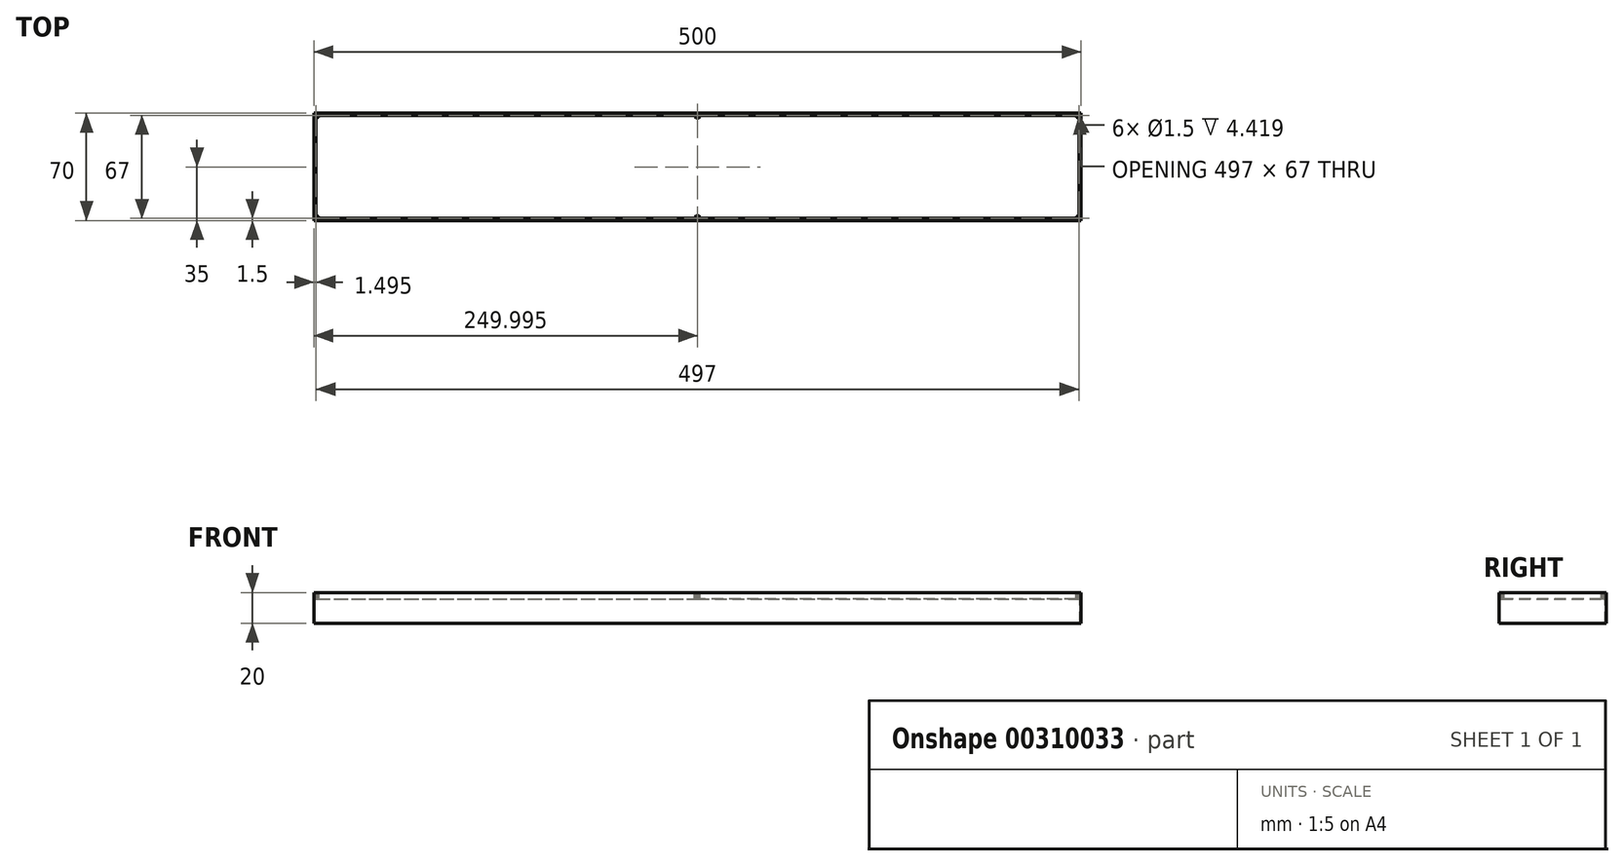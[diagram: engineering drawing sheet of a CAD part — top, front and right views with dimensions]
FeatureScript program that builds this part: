
annotation { "Feature Type Name" : "Feature", "Feature Type Description" : "" }
export const myFeature = defineFeature(function(context is Context, id is Id, definition is map)
    precondition{}
    {
        {
            var Q0;
            Q0=qCreatedBy(makeId("Front.planeOp"),FACE);
            var sketch = newSketch(context, id + "F0", { "sketchPlane" : qUnion([Q0])});
            skLineSegment(sketch, "E0.bottom", {"start": v(0.32, 0.32) * mm, "end": v(500.32, 0.32) * mm});
            skLineSegment(sketch, "E0.top", {"start": v(0.32, -19.68) * mm, "end": v(500.32, -19.68) * mm});
            skLineSegment(sketch, "E0.left", {"start": v(0.32, 0.32) * mm, "end": v(0.32, -19.68) * mm});
            skLineSegment(sketch, "E0.right", {"start": v(500.32, 0.32) * mm, "end": v(500.32, -19.68) * mm});
            skSolve(sketch);
        }
        {
            var Q0;
            Q0=makeQuery(id+"F0.imprint","IMPRINT",FACE,{"disambiguationData":[TD([[makeQuery(id+"F0.imprint","IMPRINT",EDGE,{"derivedFrom":sQuery(id+"F0.wireOp",EDGE,"E0.bottom")}),-1.0]])]});
            extrude(context, id + "F1", {"entities" : qUnion([Q0]), "depth" : 70 * mm});
        }
        {
            var Q0;
            Q0=qCreatedBy(makeId("Top.planeOp"),FACE);
            var sketch = newSketch(context, id + "F2", { "sketchPlane" : qUnion([Q0])});
            skLineSegment(sketch, "E1.1", {"start": v(498.82, -66.75) * mm, "end": v(498.82, -3.25) * mm});
            skLineSegment(sketch, "E1.3", {"start": v(1.82, -3.25) * mm, "end": v(1.82, -66.75) * mm});
            skCircle(sketch, "E2", {"center": v(1.82, -1.5) * mm, "radius": 0.75 * mm});
            skCircle(sketch, "E3", {"center": v(1.82, -68.5) * mm, "radius": 0.75 * mm});
            skCircle(sketch, "E4", {"center": v(250.32, -68.5) * mm, "radius": 0.75 * mm});
            skCircle(sketch, "E5", {"center": v(250.32, -1.5) * mm, "radius": 0.75 * mm});
            skCircle(sketch, "E6", {"center": v(498.82, -1.5) * mm, "radius": 0.75 * mm});
            skCircle(sketch, "E7", {"center": v(498.82, -68.5) * mm, "radius": 0.75 * mm});
            skArc(sketch, "E8.trimOffspring", {"start": v(497.07, -1.5) * mm, "mid": v(497.58, -2.74) * mm, "end": v(498.82, -3.25) * mm});
            skLineSegment(sketch, "E9.trimOffspring", {"start": v(497.07, -1.5) * mm, "end": v(252.07, -1.5) * mm});
            skArc(sketch, "E10.0", {"start": v(498.82, -66.75) * mm, "mid": v(497.58, -67.26) * mm, "end": v(497.07, -68.5) * mm});
            skArc(sketch, "E11.0", {"start": v(252.07, -68.5) * mm, "mid": v(250.32, -66.75) * mm, "end": v(248.57, -68.5) * mm});
            skLineSegment(sketch, "E12.trimOffspring", {"start": v(252.07, -68.5) * mm, "end": v(497.07, -68.5) * mm});
            skArc(sketch, "E13.0", {"start": v(3.57, -68.5) * mm, "mid": v(3.05, -67.26) * mm, "end": v(1.82, -66.75) * mm});
            skLineSegment(sketch, "E14.trimOffspring", {"start": v(3.57, -68.5) * mm, "end": v(248.57, -68.5) * mm});
            skArc(sketch, "E15.0", {"start": v(1.82, -3.25) * mm, "mid": v(3.05, -2.74) * mm, "end": v(3.57, -1.5) * mm});
            skArc(sketch, "E16.0", {"start": v(248.57, -1.5) * mm, "mid": v(250.32, -3.25) * mm, "end": v(252.07, -1.5) * mm});
            skLineSegment(sketch, "E17.trimOffspring", {"start": v(248.57, -1.5) * mm, "end": v(3.57, -1.5) * mm});
            skPoint(sketch, "E18.0.1.start.orphan", {"position": v(0.32, 0) * mm});
            skPoint(sketch, "E18.0.2.start.orphan", {"position": v(0.32, -70) * mm});
            skPoint(sketch, "E18.0.3.end.orphan", {"position": v(500.32, 0) * mm});
            skPoint(sketch, "E18.0.3.start.orphan", {"position": v(500.32, -70) * mm});
            skSolve(sketch);
        }
        {
            var Q0;
            Q0 = qSketchRegion(id + "F2", true);
            extrude(context, id + "F3", {"entities" : qUnion([Q0]), "operationType" : NewBodyOperationType.REMOVE, "oppositeDirection" : true, "depth" : 25 * mm, "hasSecondDirection" : true, "secondDirectionOppositeDirection" : false, "secondDirectionDepth" : 25 * mm});
        }
        {
            var Q0;
            Q0=qCreatedBy(makeId("Top.planeOp"),FACE);
            var sketch = newSketch(context, id + "F4", { "sketchPlane" : qUnion([Q0])});
            skLineSegment(sketch, "E19.0", {"start": v(0.32, 0) * mm, "end": v(500.32, 0) * mm});
            skLineSegment(sketch, "E20.0", {"start": v(1.07, -0.75) * mm, "end": v(499.57, -0.75) * mm});
            skLineSegment(sketch, "E20.1", {"start": v(1.07, -69.25) * mm, "end": v(1.07, -0.75) * mm});
            skLineSegment(sketch, "E20.2", {"start": v(1.07, -69.25) * mm, "end": v(499.57, -69.25) * mm});
            skLineSegment(sketch, "E20.3", {"start": v(499.57, -69.25) * mm, "end": v(499.57, -0.75) * mm});
            skSolve(sketch);
        }
        {
            var Q0;
            Q0 = qSketchRegion(id + "F4", true);
            extrude(context, id + "F5", {"entities" : qUnion([Q0]), "operationType" : NewBodyOperationType.REMOVE, "oppositeDirection" : true, "depth" : 21.4 * mm, "hasSecondDirection" : true, "secondDirectionOppositeDirection" : true, "secondDirectionDepth" : 4.1 * mm});
        }
    });
